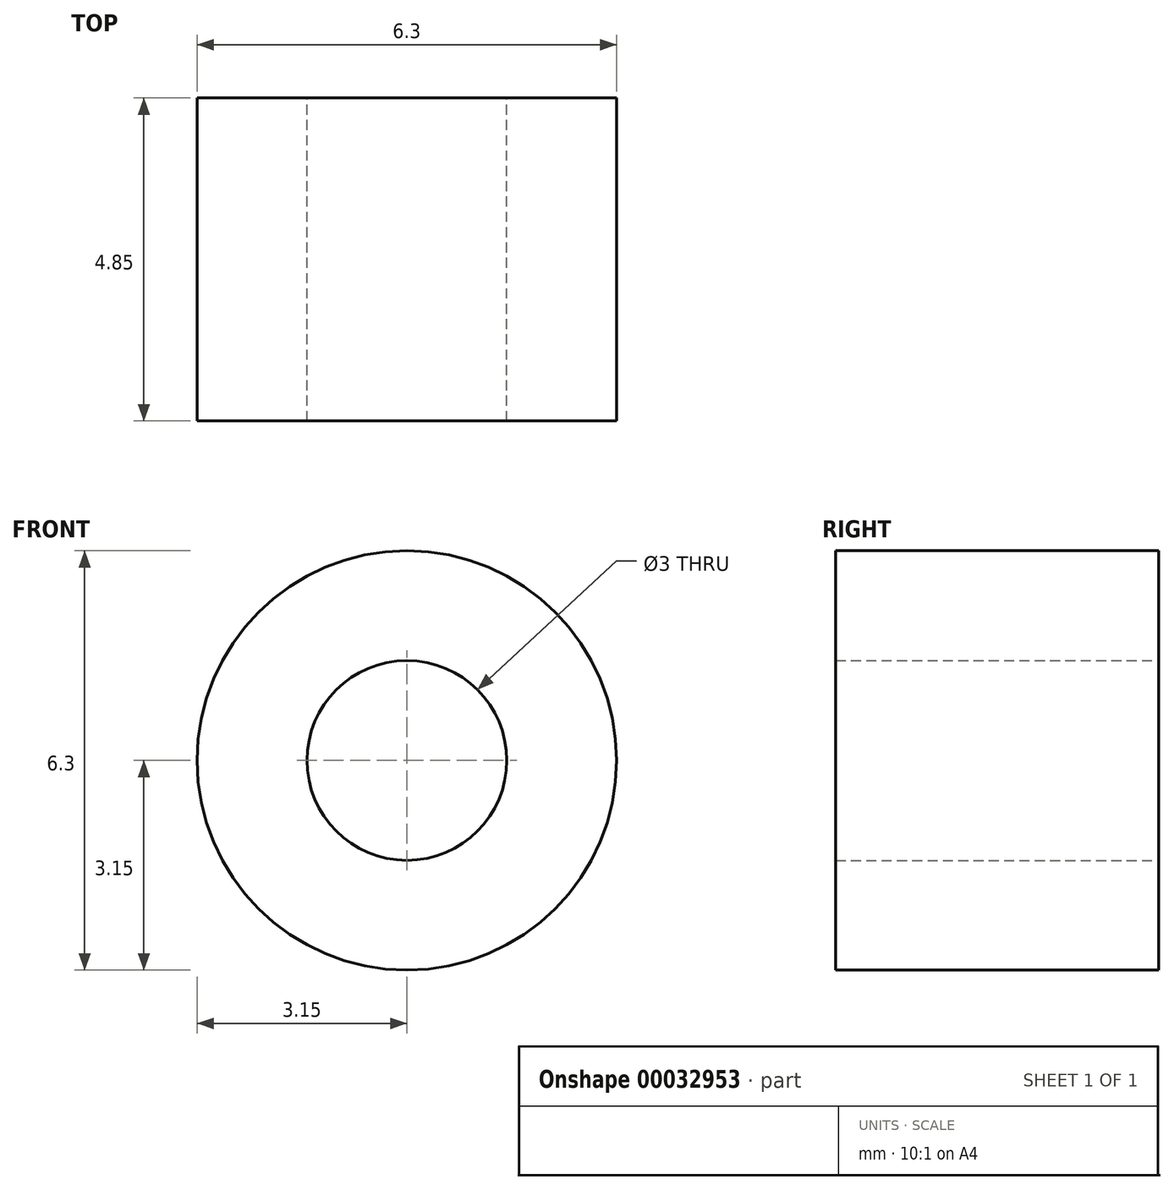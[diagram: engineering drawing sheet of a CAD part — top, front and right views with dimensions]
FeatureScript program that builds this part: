
annotation { "Feature Type Name" : "Feature", "Feature Type Description" : "" }
export const myFeature = defineFeature(function(context is Context, id is Id, definition is map)
    precondition{}
    {
        {
            var Q0;
            Q0=qCreatedBy(makeId("Front.planeOp"),FACE);
            var sketch = newSketch(context, id + "F0", { "sketchPlane" : qUnion([Q0])});
            skCircle(sketch, "E0", {"center": v(0, 0) * mm, "radius": 1.5 * mm});
            skCircle(sketch, "E1", {"center": v(0, 0) * mm, "radius": 3.15 * mm});
            skSolve(sketch);
        }
        {
            var Q0;
            Q0=qSketchRegion(id+"F0",true);
            extrude(context, id + "F1", {"entities" : qUnion([Q0]), "depth" : 4.85 * mm});
        }
    });
